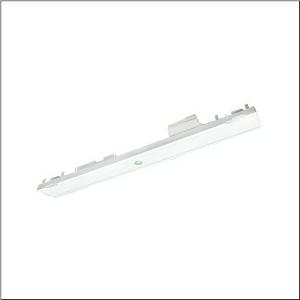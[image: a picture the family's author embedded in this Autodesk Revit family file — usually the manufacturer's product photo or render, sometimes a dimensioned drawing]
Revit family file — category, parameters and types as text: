
# Revit family: licross_r_56tl157c4x31_efa4
name_source: partatom
category: Lighting Fixtures
units: mm (PartAtom-declared; Revit-internal decimal feet)

## family parameters
Cut with Voids When Loaded = No
Host = Face
Light Source = No
Part Type = Normal
Room Calculation Point = No
Round Connector Dimension = Use Diameter
Shared = No

## types (1)
- Licross® (1 x LED, 320 lm, 3.9 W, 4000K)
    Apparent Load = 4 VA
    CIE Flux Codes = 31 68 99 100 100
    Color Rendering = 70
    Color Temperature = 4000K
    Default Elevation = 1800 mm
    Description = Licross®, luminaire insert, of sheet steel, coil coated, white, length: 500mm, width: 59mm, height: 60mm, mounting height: 2.5..7m, emergency light element,LED rated luminous flux: 320lm, light colour: 740, control gear: CEAG, with plug, 6-pole, with phase selection, mains connection: 220..240V, AC/DC, 0/50..60Hz, rated input power: 3.9W, halogen-free wiring, for trunking rail, 9..14-core, for emergency light function, supply monitoring module CEAG, with address switch, choice between two emergency light lines via tool-free moving of contact pin prior to installation in trunking rail, primary light control with lens, of PMMA, primary optical cover: cover, of PMMA, light emission: direct distribution, primary light characteristic: symmetric,  for area, compatible with all CEAG STAR technology systems (ZB-S, DG-S (DualGuard-S), LP-STAR, AT-S+), protection rating (complete): IP40, insulation class (complete): insulation class I (protective earthing), certification: CE, UKCA, protection symbol: D if used in an environment without relevant dust loads, impact resistance: IK06, permissible ambient temperature for indoor applications: -20..+40°C, packaging unit: 1 piece
    Height = 60 mm  [stored 0.19685 ft]
    Lamp = 1 x LED
    Lamp Light Flux = 320 lm
    Lamp Power = 3.9 W
    Lamp count = 1
    Length = 500 mm
    Luminous efficacy = 82 lm/W
    Manufacturer = Siteco
    ModVariant = No
    Model = 56TL157C4X31
    Mounting Place = Ceiling
    Mounting Type = Pendant
    Number of Poles = 1
    OnlyDefault = Yes
    Power Factor = 1
    Product Name = Licross®
    Product group = luminaire insert
    ProductGroupID = 902
    Protection Class = Protection class I
    Protection Degree = IP 40
    RLX_Detail_Level = 1
    RLX_Emergency_Light_Flux = 0 lm
    RLX_Emergency_Type = 0
    RLX_Emergency_Type_DB = No
    RlxData = <blob elided: 14325 chars, md5=a0596f9d>
    Socket = socket
    Standby Power = 0 W
    System Light Flux = 320 lm
    System Power = 4 W
    Type Comments = Product without accessories
    Type Image = l_1251804.jpg
    URL = http://relux.com
    VarID = ---
    Voltage = 0 V
    Weight = 0.00 kg
    Width = 59 mm

note: [stored X ft] marks values corroborated as IEEE doubles in the binary element streams (Revit-internal decimal feet)

## geometry (parser evidence)
native form markers: Sweep x11
no freeform markers — native parametric forms only
